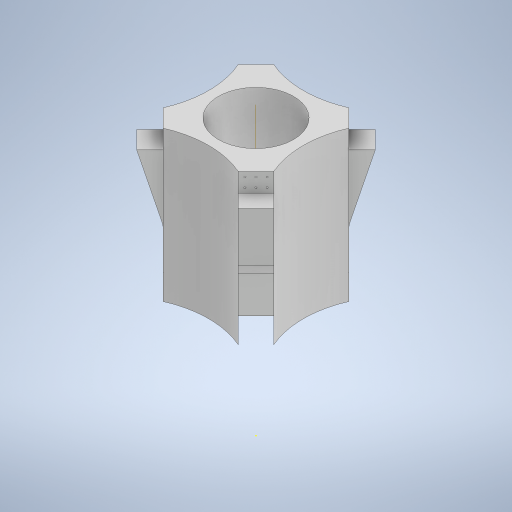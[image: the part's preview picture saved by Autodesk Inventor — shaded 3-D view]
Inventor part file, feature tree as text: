
AUTODESK INVENTOR PART (.ipt)
format: ipt  version: 2023 (Build 270158000, 158)  size: 493,568 bytes
history: native  units: in
note: dims shown in document units (in); Inventor stores cm internally (conversion verified against a paired STEP export)
features: sketch x10, extrude x6, plane x3, pattern_circular x3, projected_geometry x2, other x1, revolve x1, loft x1, fillet x1
ambient origin geometry x8: Origin, YZ Plane, XZ Plane, XY Plane, X Axis, Y Axis, Z Axis, Center Point
bodies: Solid1 (feature_tree)
feature tree (28):
  sketch  "Sketch1"  dims[d0=54.0in d1=54.0in]
  sketch  "Sketch2"  dims[d2=1.0in d3=1.0in]
  extrude  "Extrusion1"  Depth=54.0in
  plane  "Work Plane1"
  other  "Work Axis1"
  revolve  "Revolution3"  [1 undecoded]
  extrude  "Extrusion2"  Depth=0.25in
  pattern_circular  "Circular Pattern1"  [2 undecoded]
  plane  "Work Plane3"
  loft  "Loft1"
  pattern_circular  "Circular Pattern2"  [2 undecoded]
  fillet  "Fillet2"  Radius=12.0in
  extrude  "Extrusion3"  Depth=10.4855in
  extrude  "Extrusion4"  Depth=10.4855in
  extrude  "Extrusion5"  Depth=10.4855in
  pattern_circular  "Circular Pattern3"  [2 undecoded]
  extrude  "Extrusion6"  Depth=15.0in
  plane  "Work Plane2"
  sketch  "Sketch4"  dims[d34=0.25in d35=0.25in]
  sketch  "Sketch5"  dims[d36=0.25in]
  sketch  "Sketch6"  dims[d37=0.25in]
  sketch  "Sketch7"  dims[d38=0.25in]
  sketch  "Sketch8"  dims[d39=0.25in]
  projected_geometry  "Projected Loop1"
  sketch  "Sketch9"  dims[d40=0.25in]
  projected_geometry  "Projected Loop2"
  sketch  "Sketch10"  dims[d41=0.25in]
  sketch  "Sketch11"  dims[d42=2.0in d43=2.0in d44=2.0in d45=2.0in d46=12.0in d47=12.0in d48=12.0in d50=12.0in d51=15.0in d52=15.0in d53=15.0in d54=15.0in d55=17.0in d56=0.0in d64=3.0in d65=4.0in d66=360.0deg d68=0.25in d69=0.25in d70=0.25in d71=0.25in d72=0.25in d73=0.25in d74=0.75in d75=0.75in d76=0.75in d77=0.75in d78=0.75in d79=0.75in d80=0.75in d81=0.75in d82=0.75in d83=0.75in d84=2.0in d85=2.0in d86=2.0in d87=0.0in d88=1.5748in d89=360.0deg d91=-3.0in d92=3.0in d93=3.0in d94=3.5in d95=0.0in d96=90.0deg d97=0.0in d98=90.0deg d99=1.5748in d100=360.0deg d102=4.0in d103=7.0in d104=0.0in d105=3.0in d106=0.0in d107=0.25in d109=0.25in d110=0.25in d112=0.25in d113=0.25in d114=1.0in d115=1.0in d116=1.0in d117=3.0in d118=3.0in d119=1.0in d120=1.0in d121=2.0in d122=2.0in d123=3.0in d124=0.0in d125=1.5748in d126=360.0deg d128=12.0in d129=10.4855in d130=10.4855in d131=80.0in d132=0.0in]
note: 7 required parameter values undecoded (feature->parameter linkage not recoverable at this tier; creation-order binding heuristic only, values carry confidence <= 0.55)